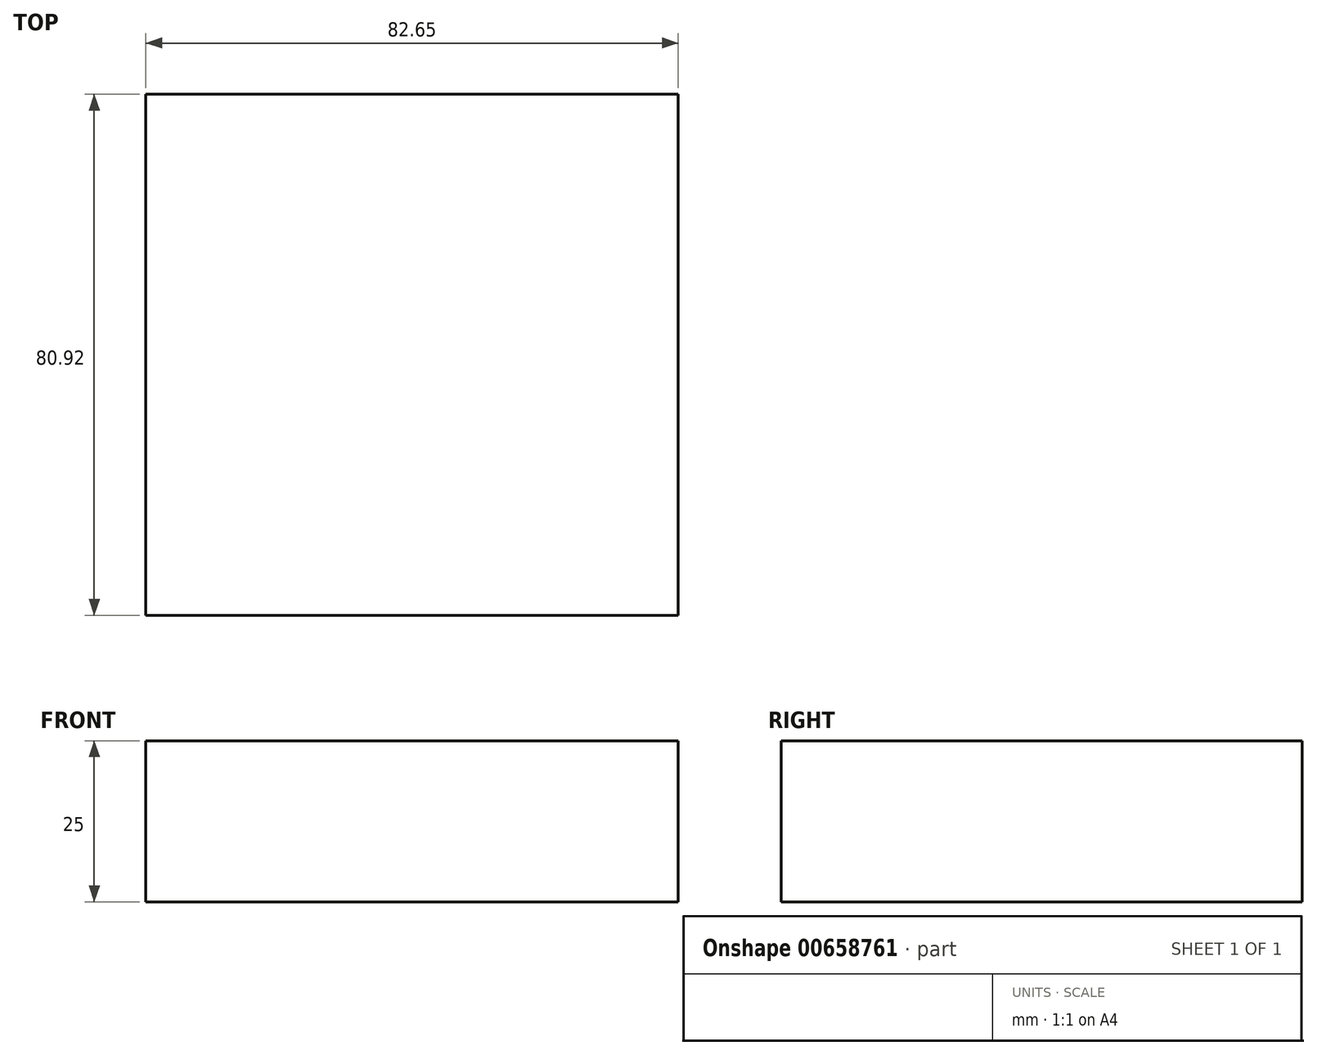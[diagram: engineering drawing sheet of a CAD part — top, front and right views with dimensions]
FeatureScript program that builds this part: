
annotation { "Feature Type Name" : "Feature", "Feature Type Description" : "" }
export const myFeature = defineFeature(function(context is Context, id is Id, definition is map)
    precondition{}
    {
        {
            var Q0;
            Q0=qCreatedBy(makeId("Top.planeOp"),FACE);
            var sketch = newSketch(context, id + "F0", { "sketchPlane" : qUnion([Q0])});
            skLineSegment(sketch, "E0.bottom", {"start": v(-38.44, 41.75) * mm, "end": v(44.2, 41.75) * mm});
            skLineSegment(sketch, "E0.top", {"start": v(-38.44, -39.17) * mm, "end": v(44.2, -39.17) * mm});
            skLineSegment(sketch, "E0.left", {"start": v(-38.44, 41.75) * mm, "end": v(-38.44, -39.17) * mm});
            skLineSegment(sketch, "E0.right", {"start": v(44.2, 41.75) * mm, "end": v(44.2, -39.17) * mm});
            skSolve(sketch);
        }
        {
            var Q0;
            Q0=makeQuery(id+"F0.imprint","IMPRINT",FACE,{"disambiguationData":[TD([[makeQuery(id+"F0.imprint","IMPRINT",EDGE,{"derivedFrom":sQuery(id+"F0.wireOp",EDGE,"E0.bottom")}),-1.0]])]});
            var Q1;
            Q1 = qSketchRegion(id + "F0", true);
            extrude(context, id + "F1", {"entities" : qUnion([Q0, Q1]), "depth" : 25 * mm, "offsetDistance" : 25 * mm});
        }
    });
